# Revit family: VLGFP0501-xxxSI8xxAxxxx
name_source: partatom
category: Oprawy oświetleniowe
revit_build: Autodesk Revit 2017 (Build: 20190508_0315(x64)
units: mm (PartAtom-declared; Revit-internal decimal feet)

## family parameters
Numer OmniClass = 23.80.70.11
Obiekt nadrzędny = Powierzchnia
Punkt obliczania pomieszczeń = Nie
Tnij formami wycięć po wczytaniu = Nie
Typ części = Normalny
Tytuł OmniClass = Luminaries for Internal Lighting
Współdzielony = Nie
Wymiar okrągłego złącza = Użyj średnicy
Źródło światła = Tak

## types (8) — shared parameters
Emituj kształt widoczny w renderingu = Nie
Emituj z długości prostokąta = 63 mm  [stored 0.206693 ft]
Emituj z szerokości prostokąta = 469 mm
Filtr koloru = 16777215
Kod zespołu = D5020200
Lampa = LED
Obciążenie pozorne = 18 VA
Odchylenie kierunku = 90.00°
Plik sieci fotometrycznej = VLGFP1501-5NDWS840A0750.IES
Producent = RIDI Leuchten GmbH
URL = www.ridi.de
Zmiana temperatury barwowej przyciemniania lampy = <Brak>
brand = RIDI
conformity mark = CE
electrical safety class = 1
height = 66 mm  [stored 0.216535 ft]
ingress protection (IP) code = IP54
length = 500 mm  [stored 1.64042 ft]
nominal frequency = 50-60Hz
nominal voltage = 230
rated input power = 18
voltage type (AC, DC, UC) = AC
weight = 0.8kg
width = 67 mm
zero-valued in all types: Domyślna rzędna

## per-type parameters (varying)
| type | Model | product name |
| VLGFP0501-5NDSI830A0250 | 1551022SI | VLGFP0501-5NDSI830A0250 |
| VLGFP0501-7DASI830A0250 | 1561022SI | VLGFP0501-7DASI830A0250 |
| VLGFP0501-5NDSI840A0250 | 1551001SI | VLGFP0501-5NDSI840A0250 |
| VLGFP0501-7DASI840A0250 | 1561001SI | VLGFP0501-7DASI840A0250 |
| VLGFP0501-5NDSI850A0250 | 1551040SI | VLGFP0501-7DASI840A0250 |
| VLGFP0501-7DASI850A0250 | 1561040SI | VLGFP0501-7DASI840A0250 |
| VLGFP0501-5NDSI865A0250 | 1551053SI | VLGFP0501-5NDSI865A0250 |
| VLGFP0501-7DASI865A0250 | 1561053SI | VLGFP0501-7DASI865A0250 |

note: [stored X ft] marks values corroborated as IEEE doubles in the binary element streams (Revit-internal decimal feet)
